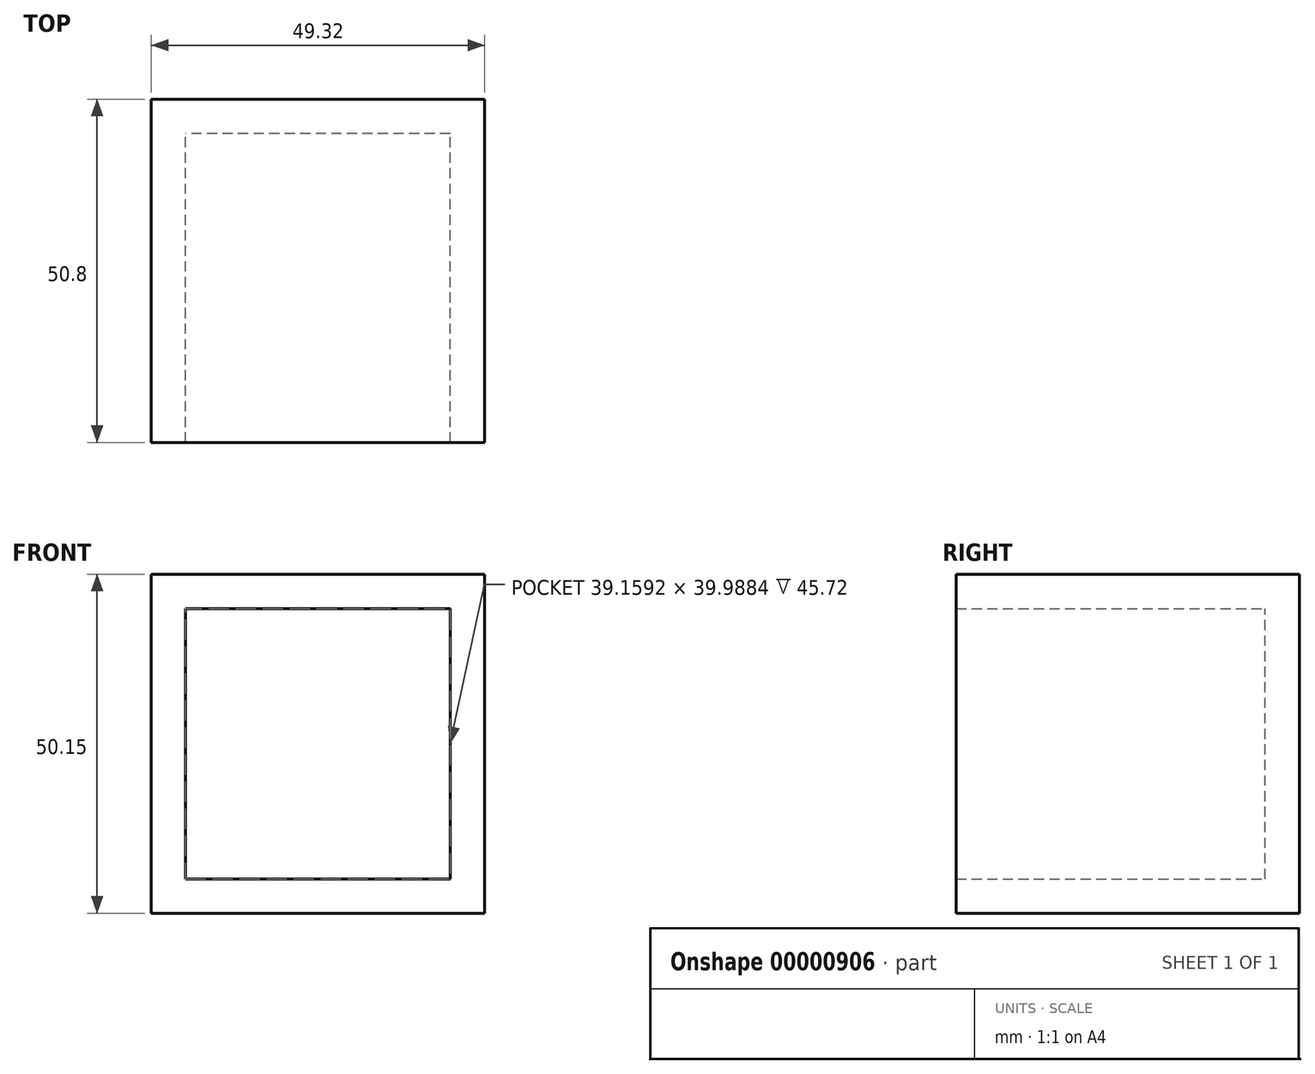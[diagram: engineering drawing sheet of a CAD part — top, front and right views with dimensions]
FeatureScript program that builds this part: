
annotation { "Feature Type Name" : "Feature", "Feature Type Description" : "" }
export const myFeature = defineFeature(function(context is Context, id is Id, definition is map)
    precondition{}
    {
        {
            var Q0;
            Q0=qCreatedBy(makeId("Front.planeOp"),FACE);
            var sketch = newSketch(context, id + "F2", { "sketchPlane" : qUnion([Q0])});
            skLineSegment(sketch, "E0", {"start": v(0, 0) * mm, "end": v(0, 50.15) * mm});
            skLineSegment(sketch, "E1", {"start": v(0, 50.15) * mm, "end": v(49.32, 50.15) * mm});
            skLineSegment(sketch, "E2", {"start": v(49.32, 50.15) * mm, "end": v(49.32, 0) * mm});
            skLineSegment(sketch, "E3", {"start": v(49.32, 0) * mm, "end": v(0, 0) * mm});
            skSolve(sketch);
        }
        {
            var Q0;
            Q0=makeQuery(id+"F2.imprint","IMPRINT",FACE,{"disambiguationData":[TD([[makeQuery(id+"F2.imprint","IMPRINT",EDGE,{"derivedFrom":sQuery(id+"F2.wireOp",EDGE,"E0")}),-1.0]])]});
            extrude(context, id + "F0", {"entities" : qUnion([Q0]), "depth" : 25.4 * mm, "hasSecondDirection" : true, "secondDirectionOppositeDirection" : true, "secondDirectionDepth" : 25.4 * mm});
        }
        {
            var Q0;
            Q0=makeQuery(id+"F0.opExtrude","CAP_FACE",FACE,{"disambiguationData":[OSD([sQuery(id+"F2.wireOp",EDGE,"E0"),sQuery(id+"F2.wireOp",EDGE,"E1"),sQuery(id+"F2.wireOp",EDGE,"E2"),sQuery(id+"F2.wireOp",EDGE,"E3")])],"isStart":false});
            shell(context, id + "F1", {"entities" : qUnion([Q0]), "thickness" : 5.08 * mm});
        }
    });
